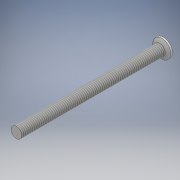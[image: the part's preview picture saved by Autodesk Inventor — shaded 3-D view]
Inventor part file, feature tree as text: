
AUTODESK INVENTOR PART (.ipt)
format: ipt  version: 2018 (Build 220112000, 112)  size: 147,968 bytes
history: native  units: mm
features: sketch x2, revolve x1, extrude x1, thread x1, chamfer x1
ambient origin geometry x8: Origin, YZ Plane, XZ Plane, XY Plane, X Axis, Y Axis, Z Axis, Center Point
bodies: Solid1 (feature_tree)
feature tree (6):
  revolve  "Revolution1"  [1 undecoded]
  extrude  "Extrusion1"  Depth=2.0mm
  thread  "Thread1"  [1 undecoded]
  chamfer  "Chamfer1"  Distance=1.2mm
  sketch  "Sketch1"  dims[d0=1.5mm d1=41.0mm]
  sketch  "Sketch2"  dims[d2=2.5mm d3=40.0mm d4=90.0deg d5=1.2mm d6=1.2mm d8=0.4mm d9=40.0mm d11=360.0deg d13=0.5mm d14=0.0mm d15=0.5mm d16=10.0mm d17=0.0mm d18=0.1mm d19=2.0mm d20=45.0deg]
note: 2 required parameter values undecoded (feature->parameter linkage not recoverable at this tier; creation-order binding heuristic only, values carry confidence <= 0.55)